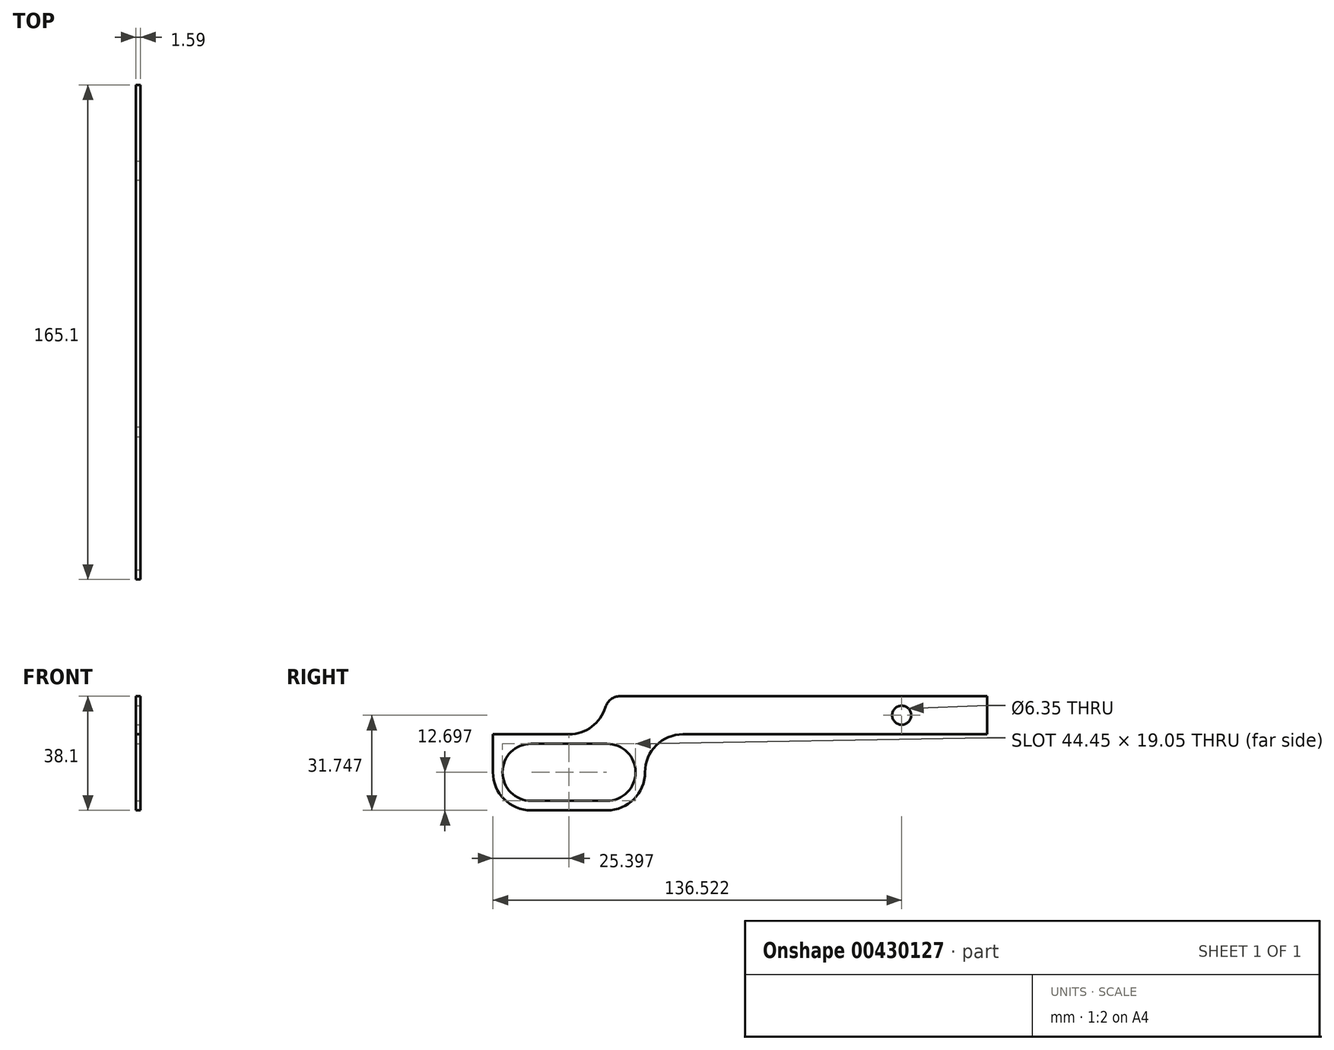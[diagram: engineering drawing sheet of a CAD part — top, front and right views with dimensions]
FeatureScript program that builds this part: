
annotation { "Feature Type Name" : "Feature", "Feature Type Description" : "" }
export const myFeature = defineFeature(function(context is Context, id is Id, definition is map)
    precondition{}
    {
        {
            var Q0;
            Q0=qCreatedBy(makeId("Right.planeOp"),FACE);
            var sketch = newSketch(context, id + "F0", { "sketchPlane" : qUnion([Q0])});
            skLineSegment(sketch, "E0", {"start": v(-79.31, 42.38) * mm, "end": v(85.79, 42.38) * mm});
            skLineSegment(sketch, "E1", {"start": v(85.79, 42.38) * mm, "end": v(85.79, 29.68) * mm});
            skLineSegment(sketch, "E2", {"start": v(85.79, 29.68) * mm, "end": v(-28.51, 29.68) * mm});
            skLineSegment(sketch, "E3", {"start": v(-28.51, 29.68) * mm, "end": v(-28.51, 4.28) * mm});
            skLineSegment(sketch, "E4", {"start": v(-28.51, 4.28) * mm, "end": v(-79.31, 4.28) * mm});
            skLineSegment(sketch, "E5", {"start": v(-79.31, 4.28) * mm, "end": v(-79.31, 42.38) * mm});
            skSolve(sketch);
        }
        {
            var Q0;
            Q0=makeQuery(id+"F0.imprint","IMPRINT",FACE,{"disambiguationData":[TD([[makeQuery(id+"F0.imprint","IMPRINT",EDGE,{"derivedFrom":sQuery(id+"F0.wireOp",EDGE,"E0")}),-1.0]])]});
            extrude(context, id + "F1", {"entities" : qUnion([Q0]), "depth" : 1.59 * mm});
        }
        {
            var Q0;
            Q0=makeQuery(id+"F1.opExtrude","CAP_FACE",FACE,{"disambiguationData":[OSD([sQuery(id+"F0.wireOp",EDGE,"E0"),sQuery(id+"F0.wireOp",EDGE,"E1"),sQuery(id+"F0.wireOp",EDGE,"E2"),sQuery(id+"F0.wireOp",EDGE,"E3"),sQuery(id+"F0.wireOp",EDGE,"E4"),sQuery(id+"F0.wireOp",EDGE,"E5")])],"isStart":false});
            var sketch = newSketch(context, id + "F2", { "sketchPlane" : qUnion([Q0])});
            skLineSegment(sketch, "E6", {"start": v(-79.31, 42.38) * mm, "end": v(-41.21, 42.38) * mm});
            skLineSegment(sketch, "E7", {"start": v(-41.21, 42.38) * mm, "end": v(-41.21, 29.68) * mm});
            skLineSegment(sketch, "E8", {"start": v(-41.21, 29.68) * mm, "end": v(-79.31, 29.68) * mm});
            skLineSegment(sketch, "E9", {"start": v(-79.31, 29.68) * mm, "end": v(-79.31, 42.38) * mm});
            skSolve(sketch);
        }
        {
            var Q0;
            Q0 = qSketchRegion(id + "F2", true);
            extrude(context, id + "F3", {"entities" : qUnion([Q0]), "operationType" : NewBodyOperationType.REMOVE, "oppositeDirection" : true, "depth" : 25.4 * mm});
        }
        {
            var Q0;
            Q0=makeQuery(id+"F3.boolean.opBoolean","COPY",EDGE,{"derivedFrom":makeQuery(id+"F3.opExtrude","SWEPT_EDGE",EDGE,{"disambiguationData":[OSD([sQuery(id+"F0.wireOp",EDGE,"E5"),sQuery(id+"F2.wireOp",EDGE,"E8"),sQuery(id+"F2.wireOp",EDGE,"E9")])]})});
            var Q1;
            Q1=makeQuery(id+"F1.opExtrude","SWEPT_EDGE",EDGE,{"disambiguationData":[OSD([sQuery(id+"F0.wireOp",EDGE,"E4"),sQuery(id+"F0.wireOp",EDGE,"E5")])]});
            var Q2;
            Q2=makeQuery(id+"F3.boolean.opBoolean","COPY",EDGE,{"derivedFrom":makeQuery(id+"F3.opExtrude","SWEPT_EDGE",EDGE,{"disambiguationData":[OSD([sQuery(id+"F2.wireOp",EDGE,"E7"),sQuery(id+"F2.wireOp",EDGE,"E8")])]})});
            var Q3;
            Q3=makeQuery(id+"F1.opExtrude","SWEPT_EDGE",EDGE,{"disambiguationData":[OSD([sQuery(id+"F0.wireOp",EDGE,"E3"),sQuery(id+"F0.wireOp",EDGE,"E4")])]});
            var Q4;
            Q4=makeQuery(id+"F1.opExtrude","SWEPT_EDGE",EDGE,{"disambiguationData":[OSD([sQuery(id+"F0.wireOp",EDGE,"E2"),sQuery(id+"F0.wireOp",EDGE,"E3")])]});
            fillet(context, id + "F4", {"entities" : qUnion([Q0, Q1, Q2, Q3, Q4]), "radius" : 12.7 * mm, "tangentPropagation" : true, "allowEdgeOverflow" : false});
        }
        {
            var Q0;
            Q0=makeQuery(id+"F4.opFillet","BLEND_EDGE",EDGE,{"blendedFrom":[makeQuery(id+"F3.boolean.opBoolean","COPY",EDGE,{"derivedFrom":makeQuery(id+"F3.opExtrude","SWEPT_EDGE",EDGE,{"disambiguationData":[OSD([sQuery(id+"F2.wireOp",EDGE,"E7"),sQuery(id+"F2.wireOp",EDGE,"E8")])]})}),makeQuery(id+"F1.opExtrude","SWEPT_FACE",FACE,{"disambiguationData":[OSD([sQuery(id+"F0.wireOp",EDGE,"E0")])]})],"blendedInto":[makeQuery(id+"F1.opExtrude","SWEPT_FACE",FACE,{"disambiguationData":[OSD([sQuery(id+"F0.wireOp",EDGE,"E0")])]})]});
            fillet(context, id + "F5", {"entities" : qUnion([Q0]), "radius" : 5.08 * mm, "tangentPropagation" : true, "allowEdgeOverflow" : false});
        }
        {
            var Q0;
            Q0=makeQuery(id+"F1.opExtrude","CAP_FACE",FACE,{"disambiguationData":[OSD([sQuery(id+"F0.wireOp",EDGE,"E0"),sQuery(id+"F0.wireOp",EDGE,"E1"),sQuery(id+"F0.wireOp",EDGE,"E2"),sQuery(id+"F0.wireOp",EDGE,"E3"),sQuery(id+"F0.wireOp",EDGE,"E4"),sQuery(id+"F0.wireOp",EDGE,"E5")])],"isStart":false});
            var sketch = newSketch(context, id + "F6", { "sketchPlane" : qUnion([Q0])});
            skCircle(sketch, "E10", {"center": v(-66.61, 16.98) * mm, "radius": 9.53 * mm});
            skSolve(sketch);
        }
        {
            var Q0;
            Q0 = qSketchRegion(id + "F6", true);
            extrude(context, id + "F7", {"entities" : qUnion([Q0]), "operationType" : NewBodyOperationType.REMOVE, "oppositeDirection" : true, "depth" : 25.4 * mm});
        }
        {
            var Q0;
            Q0=makeQuery(id+"F1.opExtrude","CAP_FACE",FACE,{"disambiguationData":[OSD([sQuery(id+"F0.wireOp",EDGE,"E0"),sQuery(id+"F0.wireOp",EDGE,"E1"),sQuery(id+"F0.wireOp",EDGE,"E2"),sQuery(id+"F0.wireOp",EDGE,"E3"),sQuery(id+"F0.wireOp",EDGE,"E4"),sQuery(id+"F0.wireOp",EDGE,"E5")])],"isStart":false});
            var sketch = newSketch(context, id + "F8", { "sketchPlane" : qUnion([Q0])});
            skCircle(sketch, "E11", {"center": v(-41.21, 16.98) * mm, "radius": 9.53 * mm});
            skSolve(sketch);
        }
        {
            var Q0;
            Q0 = qSketchRegion(id + "F8", true);
            extrude(context, id + "F9", {"entities" : qUnion([Q0]), "operationType" : NewBodyOperationType.REMOVE, "oppositeDirection" : true, "depth" : 25.4 * mm});
        }
        {
            var Q0;
            Q0=makeQuery(id+"F1.opExtrude","CAP_FACE",FACE,{"disambiguationData":[OSD([sQuery(id+"F0.wireOp",EDGE,"E0"),sQuery(id+"F0.wireOp",EDGE,"E1"),sQuery(id+"F0.wireOp",EDGE,"E2"),sQuery(id+"F0.wireOp",EDGE,"E3"),sQuery(id+"F0.wireOp",EDGE,"E4"),sQuery(id+"F0.wireOp",EDGE,"E5")])],"isStart":false});
            var sketch = newSketch(context, id + "F10", { "sketchPlane" : qUnion([Q0])});
            skLineSegment(sketch, "E12.bottom", {"start": v(-66.61, 26.5) * mm, "end": v(-41.21, 26.5) * mm});
            skLineSegment(sketch, "E12.top", {"start": v(-66.61, 7.45) * mm, "end": v(-41.21, 7.45) * mm});
            skLineSegment(sketch, "E12.left", {"start": v(-66.61, 26.5) * mm, "end": v(-66.61, 7.45) * mm});
            skLineSegment(sketch, "E12.right", {"start": v(-41.21, 26.5) * mm, "end": v(-41.21, 7.45) * mm});
            skSolve(sketch);
        }
        {
            var Q0;
            {var subQ0=sQuery(id+"F10.wireOp",EDGE,"E12.bottom");Q0=makeQuery(id+"F10.imprint","IMPRINT",FACE,{"disambiguationData":[TD([[makeQuery(id+"F10.imprint","IMPRINT",EDGE,{"derivedFrom":subQ0}),-1.0]])]});}
            extrude(context, id + "F11", {"entities" : qUnion([Q0]), "operationType" : NewBodyOperationType.REMOVE, "oppositeDirection" : true, "depth" : 25.4 * mm});
        }
        {
            var Q0;
            Q0=makeQuery(id+"F1.opExtrude","CAP_FACE",FACE,{"disambiguationData":[OSD([sQuery(id+"F0.wireOp",EDGE,"E0"),sQuery(id+"F0.wireOp",EDGE,"E1"),sQuery(id+"F0.wireOp",EDGE,"E2"),sQuery(id+"F0.wireOp",EDGE,"E3"),sQuery(id+"F0.wireOp",EDGE,"E4"),sQuery(id+"F0.wireOp",EDGE,"E5")])],"isStart":false});
            var sketch = newSketch(context, id + "F12", { "sketchPlane" : qUnion([Q0])});
            skCircle(sketch, "E13", {"center": v(57.21, 36.03) * mm, "radius": 3.18 * mm});
            skSolve(sketch);
        }
        {
            var Q0;
            Q0=makeQuery(id+"F12.imprint","IMPRINT",FACE,{"disambiguationData":[TD([[makeQuery(id+"F12.imprint","IMPRINT",EDGE,{"derivedFrom":sQuery(id+"F12.wireOp",EDGE,"E13")}),1.0]])]});
            extrude(context, id + "F13", {"entities" : qUnion([Q0]), "operationType" : NewBodyOperationType.REMOVE, "oppositeDirection" : true, "depth" : 25.4 * mm});
        }
    });
